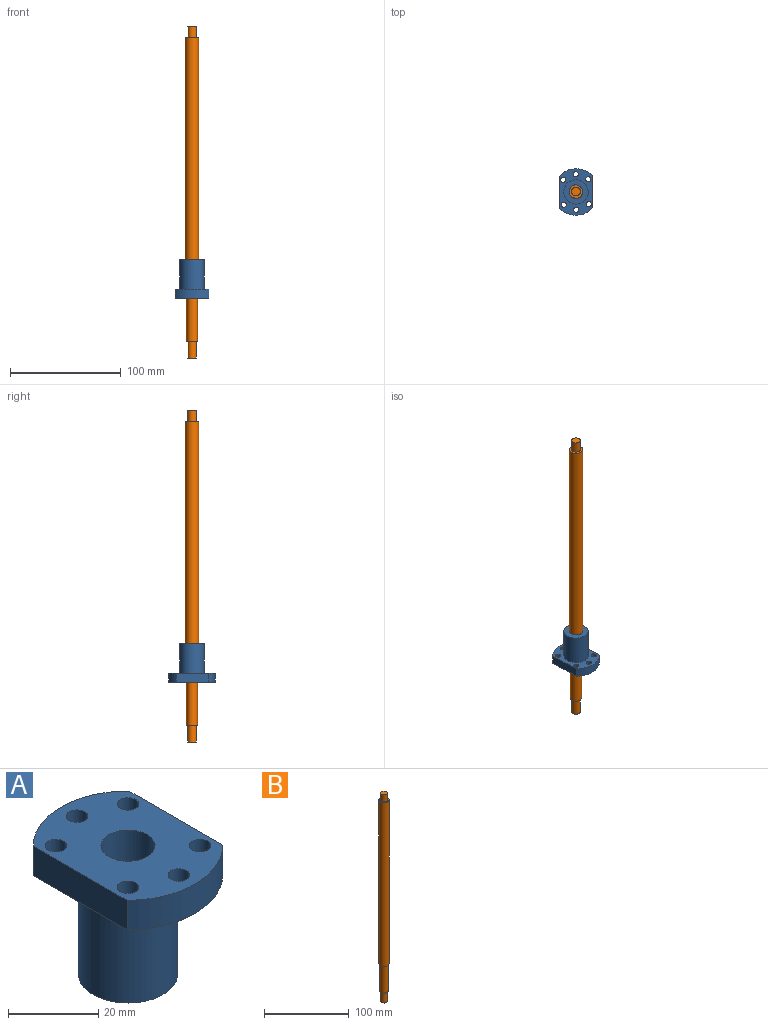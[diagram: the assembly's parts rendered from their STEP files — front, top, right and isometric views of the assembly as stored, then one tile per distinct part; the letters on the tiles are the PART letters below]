
ASSEMBLY  parts=2 mates=1
PART A: 15 faces, bbox 30x42x35 mm
  f0: plane 29.39x8mm, normal (-1,0,0), area 235.2mm2, adj f1,f4,f11,f12
  f1: cylinder r=21mm len=30mm, axis (0,0,-1), area 267.3mm2, adj f0,f2,f11,f12
  f2: plane 29.39x8mm, normal (1,0,0), area 235.2mm2, adj f1,f4,f11,f12
  f3: cylinder r=2.4mm len=8mm, axis (0,0,-1), area 120.6mm2, adj f11,f12
  f4: cylinder r=21mm len=30mm, axis (0,0,-1), area 267.3mm2, adj f0,f2,f11,f12
  f5: cylinder r=2.4mm len=8mm, axis (0,0,-1), area 120.6mm2, adj f11,f12
  f6: cylinder r=2.4mm len=8mm, axis (0,0,-1), area 120.6mm2, adj f11,f12
  f7: cylinder r=2.4mm len=8mm, axis (0,0,-1), area 120.6mm2, adj f11,f12
  f8: cylinder r=2.4mm len=8mm, axis (0,0,-1), area 120.6mm2, adj f11,f12
  f9: cylinder r=6mm len=35mm, axis (0,0,-1), area 1319.5mm2, adj f11,f14
  f10: cylinder r=2.4mm len=8mm, axis (0,0,-1), area 120.6mm2, adj f11,f12
  f11: plane 42x30mm, normal (0,0,1), area 921mm2, adj f0,f1,f2,f3,f4,f5,f6,f7
  f12: plane 42x30mm, normal (0,0,-1), area 653.9mm2, adj f0,f1,f2,f3,f4,f5,f6,f7
  f13: cylinder r=11mm len=27mm, axis (0,0,1), area 1866.1mm2, adj f12,f14
  f14: plane 22x22mm, normal (0,0,-1), area 267mm2, adj f9,f13
PART B: 9 faces, bbox 12x12x300 mm
  f0: cylinder r=6mm len=236mm, axis (0,0,1), area 8897mm2, adj f1,f8
  f1: plane 12x12mm, normal (0,0,-1), area 34.6mm2, adj f0,f2
  f2: cylinder r=5mm len=39mm, axis (0,0,1), area 1225.2mm2, adj f1,f3
  f3: plane 10x10mm, normal (0,0,-1), area 28.3mm2, adj f2,f4
  f4: cylinder r=4mm len=15mm, axis (0,0,1), area 377mm2, adj f3,f5
  f5: plane 8x8mm, normal (0,0,-1), area 50.3mm2, adj f4
  f6: plane 8x8mm, normal (0,0,1), area 50.3mm2, adj f7
  f7: cylinder r=4mm len=10mm, axis (0,0,1), area 251.3mm2, adj f6,f8
  f8: plane 12x12mm, normal (0,0,1), area 62.8mm2, adj f0,f7
PLACE A rot(axis=(0.01,-1,0),180deg) t=(-140.86,-113.24,-151.85)mm
PLACE B t=(-140.86,-113.24,-63.85)mm fixed
MATE cylindrical B.f0 <-> A.f1  axis (0,0,1) through (-140.86,-113.24,-41.85)mm
